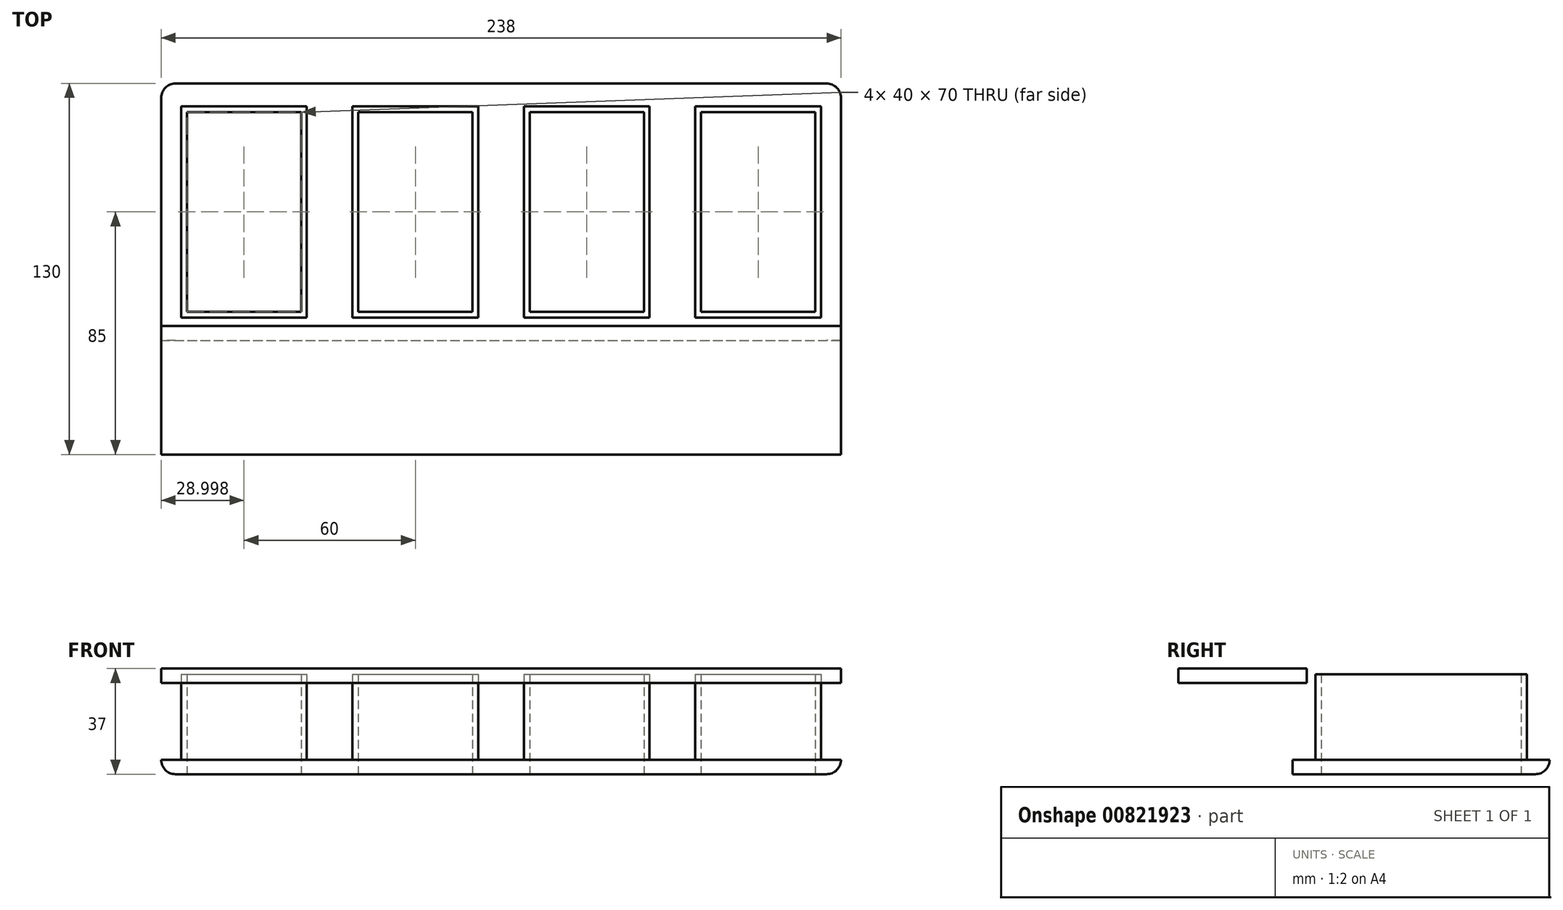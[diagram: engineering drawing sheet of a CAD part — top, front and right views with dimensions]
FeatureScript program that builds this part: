
annotation { "Feature Type Name" : "Feature", "Feature Type Description" : "" }
export const myFeature = defineFeature(function(context is Context, id is Id, definition is map)
    precondition{}
    {
        {
            var Q0;
            Q0=qCreatedBy(makeId("Top.planeOp"),FACE);
            var sketch = newSketch(context, id + "F0", { "sketchPlane" : qUnion([Q0])});
            skLineSegment(sketch, "E0.bottom", {"start": v(-131.57, 10) * mm, "end": v(106.43, 10) * mm});
            skLineSegment(sketch, "E0.top", {"start": v(-131.57, -80) * mm, "end": v(106.43, -80) * mm});
            skLineSegment(sketch, "E0.right", {"start": v(106.43, 10) * mm, "end": v(106.43, -80) * mm});
            skLineSegment(sketch, "E1.bottom", {"start": v(-122.57, 0) * mm, "end": v(-82.57, 0) * mm});
            skLineSegment(sketch, "E1.top", {"start": v(-122.57, -70) * mm, "end": v(-82.57, -70) * mm});
            skLineSegment(sketch, "E1.left", {"start": v(-122.57, 0) * mm, "end": v(-122.57, -70) * mm});
            skLineSegment(sketch, "E1.right", {"start": v(-82.57, 0) * mm, "end": v(-82.57, -70) * mm});
            skLineSegment(sketch, "E2.1.0.0", {"start": v(-62.57, 0) * mm, "end": v(-22.57, 0) * mm});
            skLineSegment(sketch, "E2.1.0.1", {"start": v(-62.57, 0) * mm, "end": v(-62.57, -70) * mm});
            skLineSegment(sketch, "E2.1.0.2", {"start": v(-62.57, -70) * mm, "end": v(-22.57, -70) * mm});
            skLineSegment(sketch, "E2.1.0.3", {"start": v(-22.57, 0) * mm, "end": v(-22.57, -70) * mm});
            skLineSegment(sketch, "E2.2.0.0", {"start": v(-2.57, 0) * mm, "end": v(37.43, 0) * mm});
            skLineSegment(sketch, "E2.2.0.1", {"start": v(-2.57, 0) * mm, "end": v(-2.57, -70) * mm});
            skLineSegment(sketch, "E2.2.0.2", {"start": v(-2.57, -70) * mm, "end": v(37.43, -70) * mm});
            skLineSegment(sketch, "E2.2.0.3", {"start": v(37.43, 0) * mm, "end": v(37.43, -70) * mm});
            skLineSegment(sketch, "E2.3.0.0", {"start": v(57.43, 0) * mm, "end": v(97.43, 0) * mm});
            skLineSegment(sketch, "E2.3.0.1", {"start": v(57.43, 0) * mm, "end": v(57.43, -70) * mm});
            skLineSegment(sketch, "E2.3.0.2", {"start": v(57.43, -70) * mm, "end": v(97.43, -70) * mm});
            skLineSegment(sketch, "E2.3.0.3", {"start": v(97.43, 0) * mm, "end": v(97.43, -70) * mm});
            skLineSegment(sketch, "E3.bottom", {"start": v(-131.57, -80) * mm, "end": v(-129.57, -80) * mm});
            skLineSegment(sketch, "E3.left", {"start": v(-131.57, -80) * mm, "end": v(-131.57, 10) * mm});
            skLineSegment(sketch, "E4.0", {"start": v(-124.57, 2) * mm, "end": v(-80.57, 2) * mm});
            skLineSegment(sketch, "E4.1", {"start": v(-124.57, 2) * mm, "end": v(-124.57, -72) * mm});
            skLineSegment(sketch, "E4.2", {"start": v(-124.57, -72) * mm, "end": v(-80.57, -72) * mm});
            skLineSegment(sketch, "E4.3", {"start": v(-80.57, 2) * mm, "end": v(-80.57, -72) * mm});
            skLineSegment(sketch, "E5.0", {"start": v(-64.57, 2) * mm, "end": v(-20.57, 2) * mm});
            skLineSegment(sketch, "E5.1", {"start": v(-64.57, 2) * mm, "end": v(-64.57, -72) * mm});
            skLineSegment(sketch, "E5.2", {"start": v(-64.57, -72) * mm, "end": v(-20.57, -72) * mm});
            skLineSegment(sketch, "E5.3", {"start": v(-20.57, 2) * mm, "end": v(-20.57, -72) * mm});
            skLineSegment(sketch, "E6.0", {"start": v(-4.57, 2) * mm, "end": v(-4.57, -72) * mm});
            skLineSegment(sketch, "E6.1", {"start": v(-4.57, 2) * mm, "end": v(39.43, 2) * mm});
            skLineSegment(sketch, "E6.2", {"start": v(39.43, 2) * mm, "end": v(39.43, -72) * mm});
            skLineSegment(sketch, "E6.3", {"start": v(-4.57, -72) * mm, "end": v(39.43, -72) * mm});
            skLineSegment(sketch, "E7.0", {"start": v(55.43, 2) * mm, "end": v(99.43, 2) * mm});
            skLineSegment(sketch, "E7.1", {"start": v(55.43, 2) * mm, "end": v(55.43, -72) * mm});
            skLineSegment(sketch, "E7.2", {"start": v(55.43, -72) * mm, "end": v(99.43, -72) * mm});
            skLineSegment(sketch, "E7.3", {"start": v(99.43, 2) * mm, "end": v(99.43, -72) * mm});
            skSolve(sketch);
        }
        {
            var Q0;
            Q0=makeQuery(id+"F0.imprint","IMPRINT",FACE,{"disambiguationData":[TD([[makeQuery(id+"F0.imprint","IMPRINT",EDGE,{"derivedFrom":sQuery(id+"F0.wireOp",EDGE,"E0.bottom")}),-1.0]])]});
            var Q1;
            Q1=makeQuery(id+"F0.imprint","IMPRINT",FACE,{"disambiguationData":[TD([[makeQuery(id+"F0.imprint","IMPRINT",EDGE,{"derivedFrom":sQuery(id+"F0.wireOp",EDGE,"E0.bottom")}),-1.0]])]});
            extrude(context, id + "F1", {"entities" : qUnion([Q0, Q1]), "depth" : 5 * mm, "offsetDistance" : 25 * mm});
        }
        {
            var Q0;
            Q0=makeQuery(id+"F1.opExtrude","SWEPT_FACE",FACE,{"disambiguationData":[OSD([sQuery(id+"F0.wireOp",EDGE,"E3.left")])]});
            var sketch = newSketch(context, id + "F2", { "sketchPlane" : qUnion([Q0])});
            skLineSegment(sketch, "E8.top", {"start": v(120, 37) * mm, "end": v(75, 37) * mm});
            skLineSegment(sketch, "E9.top", {"start": v(120, 32) * mm, "end": v(75, 32) * mm});
            skLineSegment(sketch, "E9.left", {"start": v(120, 37) * mm, "end": v(120, 32) * mm});
            skLineSegment(sketch, "E9.right", {"start": v(75, 37) * mm, "end": v(75, 32) * mm});
            skLineSegment(sketch, "E10.bottom", {"start": v(75, 32) * mm, "end": v(80, 32) * mm});
            skLineSegment(sketch, "E10.top", {"start": v(75, 5) * mm, "end": v(80, 5) * mm});
            skLineSegment(sketch, "E10.left", {"start": v(75, 32) * mm, "end": v(75, 5) * mm});
            skLineSegment(sketch, "E10.right", {"start": v(80, 32) * mm, "end": v(80, 5) * mm});
            skSolve(sketch);
        }
        {
            var Q0;
            Q0=makeQuery(id+"F2.imprint","IMPRINT",FACE,{"disambiguationData":[TD([[makeQuery(id+"F2.imprint","IMPRINT",EDGE,{"derivedFrom":sQuery(id+"F2.wireOp",EDGE,"E8.top")}),1.0]])]});
            var Q1;
            Q1=makeQuery(id+"F2.imprint","IMPRINT",FACE,{"disambiguationData":[TD([[makeQuery(id+"F2.imprint","IMPRINT",EDGE,{"derivedFrom":sQuery(id+"F2.wireOp",EDGE,"E10.bottom")}),-1.0]])]});
            extrude(context, id + "F3", {"entities" : qUnion([Q0, Q1]), "operationType" : NewBodyOperationType.ADD, "oppositeDirection" : true, "depth" : 238 * mm, "offsetDistance" : 25 * mm});
        }
        {
            var Q0;
            Q0=makeQuery(id+"F0.imprint","IMPRINT",FACE,{"disambiguationData":[TD([[makeQuery(id+"F0.imprint","IMPRINT",EDGE,{"derivedFrom":sQuery(id+"F0.wireOp",EDGE,"E1.bottom")}),1.0]])]});
            var Q1;
            Q1=makeQuery(id+"F0.imprint","IMPRINT",FACE,{"disambiguationData":[TD([[makeQuery(id+"F0.imprint","IMPRINT",EDGE,{"derivedFrom":sQuery(id+"F0.wireOp",EDGE,"E2.1.0.0")}),1.0]])]});
            var Q2;
            Q2=makeQuery(id+"F0.imprint","IMPRINT",FACE,{"disambiguationData":[TD([[makeQuery(id+"F0.imprint","IMPRINT",EDGE,{"derivedFrom":sQuery(id+"F0.wireOp",EDGE,"E2.2.0.0")}),1.0]])]});
            var Q3;
            Q3=makeQuery(id+"F0.imprint","IMPRINT",FACE,{"disambiguationData":[TD([[makeQuery(id+"F0.imprint","IMPRINT",EDGE,{"derivedFrom":sQuery(id+"F0.wireOp",EDGE,"E2.3.0.0")}),1.0]])]});
            extrude(context, id + "F4", {"entities" : qUnion([Q0, Q1, Q2, Q3]), "operationType" : NewBodyOperationType.ADD, "depth" : 35 * mm, "offsetDistance" : 25 * mm});
        }
        {
            var Q0;
            Q0=makeQuery(id+"F1.opExtrude","CAP_EDGE",EDGE,{"disambiguationData":[OSD([sQuery(id+"F0.wireOp",EDGE,"E0.bottom")])],"isStart":true});
            var Q1;
            Q1=makeQuery(id+"F1.opExtrude","CAP_EDGE",EDGE,{"disambiguationData":[OSD([sQuery(id+"F0.wireOp",EDGE,"E3.left")])],"isStart":true});
            var Q2;
            Q2=makeQuery(id+"F1.opExtrude","CAP_EDGE",EDGE,{"disambiguationData":[OSD([sQuery(id+"F0.wireOp",EDGE,"E0.right")])],"isStart":true});
            var Q3;
            Q3=makeQuery(id+"F1.opExtrude","SWEPT_EDGE",EDGE,{"disambiguationData":[OSD([sQuery(id+"F0.wireOp",EDGE,"E0.bottom"),sQuery(id+"F0.wireOp",EDGE,"E0.right")])]});
            var Q4;
            Q4=makeQuery(id+"F1.opExtrude","SWEPT_EDGE",EDGE,{"disambiguationData":[OSD([sQuery(id+"F0.wireOp",EDGE,"E0.bottom"),sQuery(id+"F0.wireOp",EDGE,"E3.left")])]});
            fillet(context, id + "F5", {"entities" : qUnion([Q0, Q1, Q2, Q3, Q4]), "radius" : 5 * mm, "tangentPropagation" : true, "allowEdgeOverflow" : false});
        }
    });
